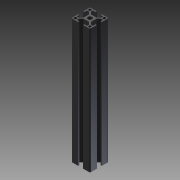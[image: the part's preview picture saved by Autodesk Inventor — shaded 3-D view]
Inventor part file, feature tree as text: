
AUTODESK INVENTOR PART (.ipt)
format: ipt  version: 2011 SP1 (Build 150282100, 282)  size: 189,440 bytes
history: native  units: mm
features: other x21, sketch x3, hole x2, extrude x1, pattern_linear x1
ambient origin geometry x8: Origin, YZ Plane, XZ Plane, XY Plane, X Axis, Y Axis, Z Axis, Center Point
bodies: Solid1 (feature_tree)
feature tree (28):
  extrude  "Extrusion1"  Depth=20.0mm
  hole  "Hole1"  [1 undecoded]
  hole  "Hole2"  [1 undecoded]
  pattern_linear  "Rectangular Pattern1"  [2 undecoded]
  other  "C1_XY"
  other  "C1_YZ"
  other  "C1_ZX"
  other  "C1_X"
  other  "C1_Y"
  other  "C1_Z"
  other  "C1_Center"
  other  "to_frame_cap1_XY"
  other  "to_frame_cap1_YZ"
  other  "to_frame_cap1_ZX"
  other  "to_frame_cap1_X"
  other  "to_frame_cap1_Y"
  other  "to_frame_cap1_Z"
  other  "to_frame_cap1_Center"
  other  "to_frame_cap2_XY"
  other  "to_frame_cap2_YZ"
  other  "to_frame_cap2_ZX"
  other  "to_frame_cap2_X"
  other  "to_frame_cap2_Y"
  other  "to_frame_cap2_Z"
  other  "to_frame_cap2_Center"
  sketch  "Sketch_1"  dims[d0=200.0mm d1=0.0mm]
  sketch  "Sketch2"  dims[d2=6.8mm d3=6.0mm d4=4.0mm d5=2.0mm d6=90.0deg d7=200.0mm d8=0.0mm]
  sketch  "Sketch3"  dims[d9=4.2mm d10=6.0mm d11=4.0mm d12=2.0mm d13=90.0deg d14=200.0mm d15=0.0mm d16=20.0mm d18=23.2mm d19=20.0mm d21=23.2mm d22=0.0mm d23=0.0mm d24=0.0mm]
note: 4 required parameter values undecoded (feature->parameter linkage not recoverable at this tier; creation-order binding heuristic only, values carry confidence <= 0.55)
